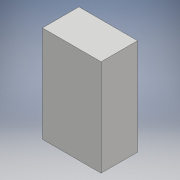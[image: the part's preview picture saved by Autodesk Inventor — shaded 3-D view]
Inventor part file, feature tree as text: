
AUTODESK INVENTOR PART (.ipt)
format: ipt  version: 2018 (Build 220112000, 112)  size: 111,104 bytes
history: native  units: mm
features: extrude x2, sketch x2
ambient origin geometry x8: Origin, YZ Plane, XZ Plane, XY Plane, X Axis, Y Axis, Z Axis, Center Point
bodies: Solid1 (feature_tree)
feature tree (4):
  extrude  "Extrusion1"  Depth=45.0mm
  extrude  "Extrusion2"  Depth=5.0mm
  sketch  "Sketch1"  dims[d0=74.0mm d1=45.0mm]
  sketch  "Sketch2"  dims[d2=28.0mm d3=0.0mm d4=5.0mm d5=5.0mm d6=12.0mm d7=4.5mm d8=3.0mm d9=4.0mm d10=0.0mm]
